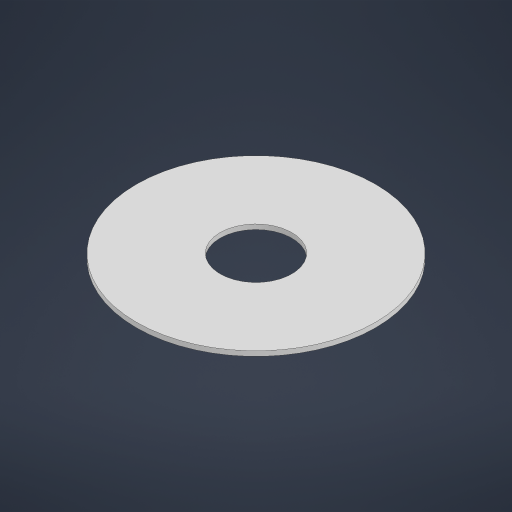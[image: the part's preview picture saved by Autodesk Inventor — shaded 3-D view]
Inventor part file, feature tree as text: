
AUTODESK INVENTOR PART (.ipt)
format: ipt  version: 2024 (Build 280153000, 153)  size: 161,280 bytes
history: native  units: mm
features: other x1, extrude x1, sketch x1
ambient origin geometry x8: Origin, YZ Plane, XZ Plane, XY Plane, X Axis, Y Axis, Z Axis, Center Point
bodies: Body1 (feature_tree)
feature tree (3):
  other  "솔리드1"
  extrude  "돌출1"  Depth=3.0mm
  sketch  "스케치1"
